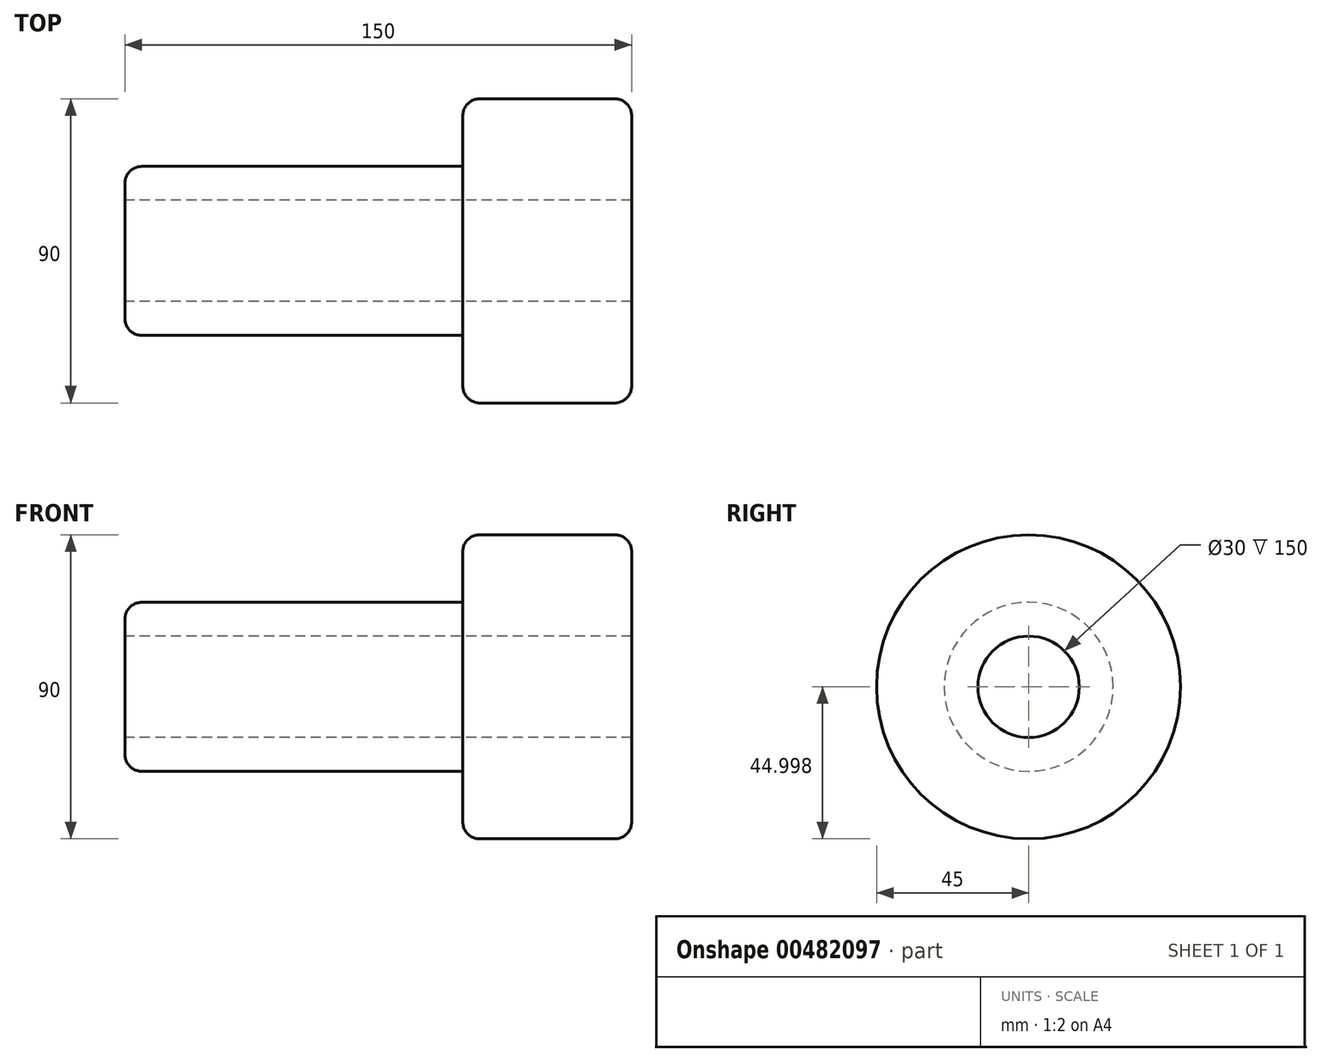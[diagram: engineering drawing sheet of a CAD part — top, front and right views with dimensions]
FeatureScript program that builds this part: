
annotation { "Feature Type Name" : "Feature", "Feature Type Description" : "" }
export const myFeature = defineFeature(function(context is Context, id is Id, definition is map)
    precondition{}
    {
        {
            var Q0;
            Q0=qCreatedBy(makeId("Right.planeOp"),FACE);
            var sketch = newSketch(context, id + "F0", { "sketchPlane" : qUnion([Q0])});
            skCircle(sketch, "E0", {"center": v(0, 39.79) * mm, "radius": 15 * mm});
            skCircle(sketch, "E1", {"center": v(0, 39.79) * mm, "radius": 25 * mm});
            skSolve(sketch);
        }
        {
            var Q0;
            Q0=makeQuery(id+"F0.imprint","IMPRINT",FACE,{"disambiguationData":[TD([[makeQuery(id+"F0.imprint","IMPRINT",EDGE,{"derivedFrom":sQuery(id+"F0.wireOp",EDGE,"E0")}),-1.0]])]});
            extrude(context, id + "F1", {"entities" : qUnion([Q0]), "depth" : 100 * mm});
        }
        {
            var Q0;
            Q0=makeQuery(id+"F1.opExtrude","CAP_FACE",FACE,{"disambiguationData":[OSD([sQuery(id+"F0.wireOp",EDGE,"E0"),sQuery(id+"F0.wireOp",EDGE,"E1")])],"isStart":false});
            var sketch = newSketch(context, id + "F2", { "sketchPlane" : qUnion([Q0])});
            skPoint(sketch, "E2", {"position": v(0, 39.79) * mm});
            skSolve(sketch);
        }
        {
            var Q0;
            Q0=makeQuery(id+"F2.imprint","IMPRINT",FACE,{"disambiguationData":[TD([[makeQuery(id+"F2.imprint","IMPRINT",EDGE,{"derivedFrom":makeQuery(id+"F1.opExtrude","CAP_EDGE",EDGE,{"disambiguationData":[OSD([sQuery(id+"F0.wireOp",EDGE,"E0")])],"isStart":false})}),-1.0]])]});
            var sketch = newSketch(context, id + "F3", { "sketchPlane" : qUnion([Q0])});
            skCircle(sketch, "E3", {"center": v(0, 39.79) * mm, "radius": 45 * mm});
            skSolve(sketch);
        }
        {
            var Q0;
            Q0=makeQuery(id+"F2.imprint","IMPRINT",FACE,{"disambiguationData":[TD([[makeQuery(id+"F2.imprint","IMPRINT",EDGE,{"derivedFrom":makeQuery(id+"F1.opExtrude","CAP_EDGE",EDGE,{"disambiguationData":[OSD([sQuery(id+"F0.wireOp",EDGE,"E0")])],"isStart":false})}),-1.0]])]});
            var Q1;
            Q1=makeQuery(id+"F3.imprint","IMPRINT",FACE,{"disambiguationData":[TD([[makeQuery(id+"F3.imprint","IMPRINT",EDGE,{"derivedFrom":sQuery(id+"F3.wireOp",EDGE,"E3")}),1.0]])]});
            extrude(context, id + "F4", {"entities" : qUnion([Q0, Q1]), "operationType" : NewBodyOperationType.ADD, "depth" : 50 * mm});
        }
        {
            var Q0;
            Q0=makeQuery(id+"F4.opExtrude","CAP_EDGE",EDGE,{"disambiguationData":[OSD([sQuery(id+"F3.wireOp",EDGE,"E3")])],"isStart":true});
            var Q1;
            Q1=makeQuery(id+"F1.opExtrude","CAP_EDGE",EDGE,{"disambiguationData":[OSD([sQuery(id+"F0.wireOp",EDGE,"E1")])],"isStart":true});
            fillet(context, id + "F5", {"entities" : qUnion([Q0, Q1]), "radius" : 5 * mm, "tangentPropagation" : true, "allowEdgeOverflow" : false});
        }
        {
            var Q0;
            Q0=makeQuery(id+"F4.opExtrude","CAP_EDGE",EDGE,{"disambiguationData":[OSD([sQuery(id+"F3.wireOp",EDGE,"E3")])],"isStart":false});
            fillet(context, id + "F6", {"entities" : qUnion([Q0]), "radius" : 5 * mm, "tangentPropagation" : true, "allowEdgeOverflow" : false});
        }
    });
